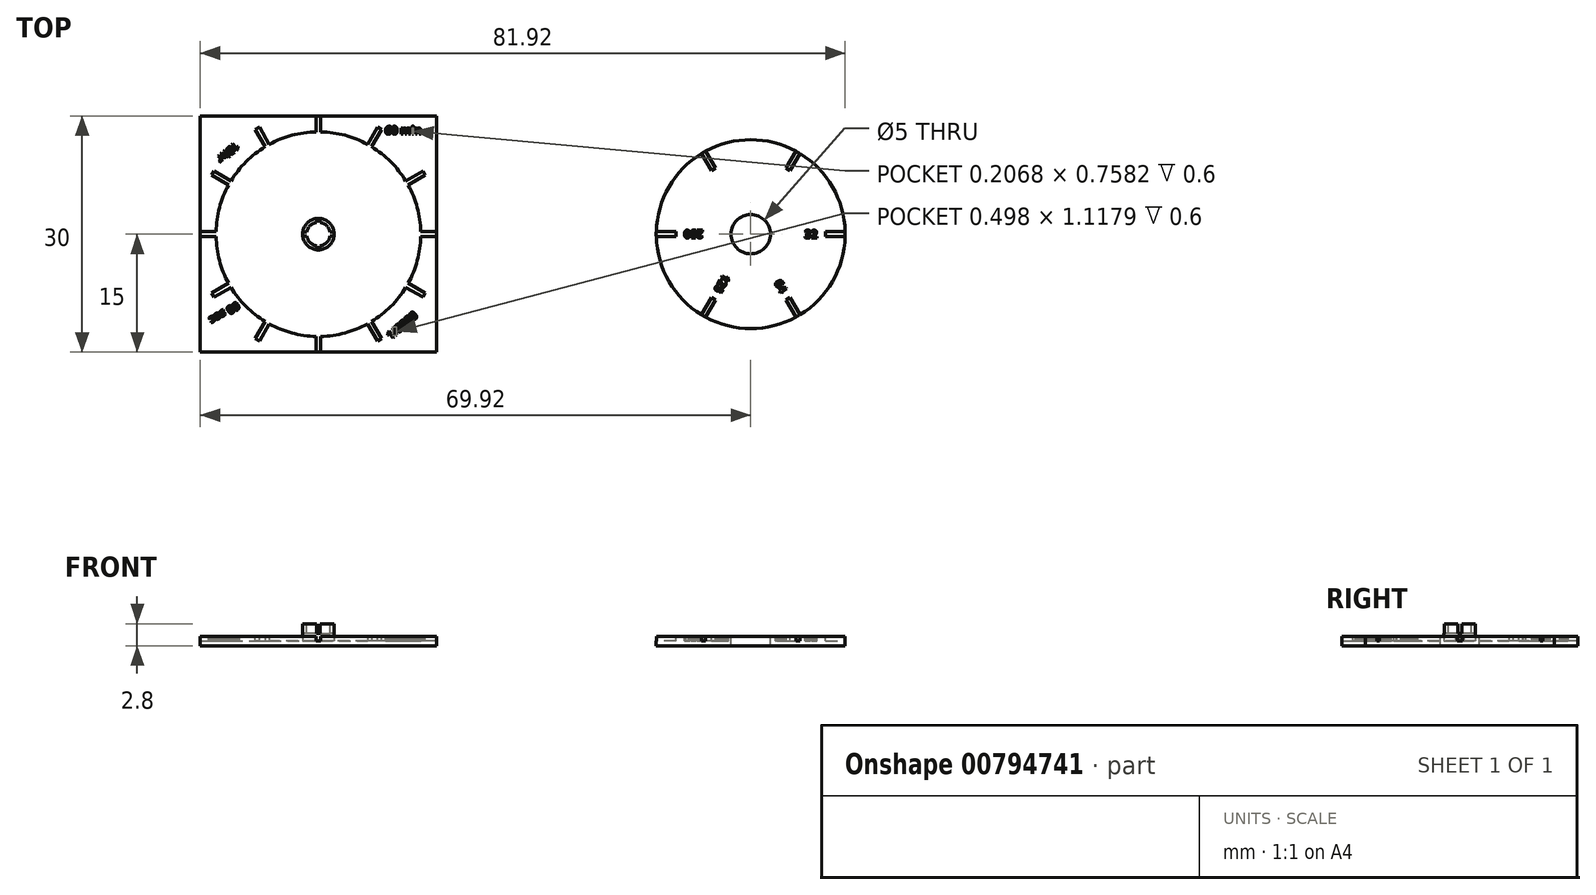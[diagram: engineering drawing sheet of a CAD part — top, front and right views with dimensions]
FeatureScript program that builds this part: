
annotation { "Feature Type Name" : "Feature", "Feature Type Description" : "" }
export const myFeature = defineFeature(function(context is Context, id is Id, definition is map)
    precondition{}
    {
        {
            var Q0;
            Q0=qCreatedBy(makeId("Top.planeOp"),FACE);
            var sketch = newSketch(context, id + "F0", { "sketchPlane" : qUnion([Q0])});
            skLineSegment(sketch, "E0.bottom", {"start": v(-15, 15) * mm, "end": v(15, 15) * mm});
            skLineSegment(sketch, "E0.top", {"start": v(-15, -15) * mm, "end": v(15, -15) * mm});
            skLineSegment(sketch, "E0.left", {"start": v(-15, 15) * mm, "end": v(-15, -15) * mm});
            skLineSegment(sketch, "E0.right", {"start": v(15, 15) * mm, "end": v(15, -15) * mm});
            skPoint(sketch, "E0.middle", {"position": v(0, 0) * mm});
            skCircle(sketch, "E1", {"center": v(0, 0) * mm, "radius": 13 * mm});
            skCircle(sketch, "E2", {"center": v(0, 0) * mm, "radius": 2 * mm});
            skCircle(sketch, "E3", {"center": v(54.92, 0) * mm, "radius": 12 * mm});
            skCircle(sketch, "E4", {"center": v(54.92, 0) * mm, "radius": 2.5 * mm});
            skSolve(sketch);
        }
        {
            var Q0;
            Q0=makeQuery(id+"F0.imprint","IMPRINT",FACE,{"disambiguationData":[TD([[makeQuery(id+"F0.imprint","IMPRINT",EDGE,{"derivedFrom":sQuery(id+"F0.wireOp",EDGE,"E0.bottom")}),-1.0]])]});
            var Q1;
            Q1=makeQuery(id+"F0.imprint","IMPRINT",FACE,{"disambiguationData":[TD([[makeQuery(id+"F0.imprint","IMPRINT",EDGE,{"derivedFrom":sQuery(id+"F0.wireOp",EDGE,"E1")}),1.0]])]});
            var Q2;
            Q2=makeQuery(id+"F0.imprint","IMPRINT",FACE,{"disambiguationData":[TD([[makeQuery(id+"F0.imprint","IMPRINT",EDGE,{"derivedFrom":sQuery(id+"F0.wireOp",EDGE,"E2")}),1.0]])]});
            var Q3;
            Q3=makeQuery(id+"F0.imprint","IMPRINT",FACE,{"disambiguationData":[TD([[makeQuery(id+"F0.imprint","IMPRINT",EDGE,{"derivedFrom":sQuery(id+"F0.wireOp",EDGE,"E3")}),1.0]])]});
            extrude(context, id + "F1", {"entities" : qUnion([Q0, Q1, Q2, Q3]), "oppositeDirection" : true, "depth" : 0.6 * mm, "offsetDistance" : 25 * mm});
        }
        {
            var Q0;
            Q0=makeQuery(id+"F0.imprint","IMPRINT",FACE,{"disambiguationData":[TD([[makeQuery(id+"F0.imprint","IMPRINT",EDGE,{"derivedFrom":sQuery(id+"F0.wireOp",EDGE,"E0.bottom")}),-1.0]])]});
            var Q1;
            Q1=makeQuery(id+"F0.imprint","IMPRINT",FACE,{"disambiguationData":[TD([[makeQuery(id+"F0.imprint","IMPRINT",EDGE,{"derivedFrom":sQuery(id+"F0.wireOp",EDGE,"E3")}),1.0]])]});
            extrude(context, id + "F2", {"entities" : qUnion([Q0, Q1]), "operationType" : NewBodyOperationType.ADD, "depth" : 0.6 * mm, "offsetDistance" : 25 * mm});
        }
        {
            var Q0;
            Q0=makeQuery(id+"F0.imprint","IMPRINT",FACE,{"disambiguationData":[TD([[makeQuery(id+"F0.imprint","IMPRINT",EDGE,{"derivedFrom":sQuery(id+"F0.wireOp",EDGE,"E2")}),1.0]])]});
            var Q1;
            Q1=makeQuery(id+"F1.opExtrude","CAP_FACE",FACE,{"disambiguationData":[OSD([sQuery(id+"F0.wireOp",EDGE,"E0.bottom"),sQuery(id+"F0.wireOp",EDGE,"E0.top"),sQuery(id+"F0.wireOp",EDGE,"E0.left"),sQuery(id+"F0.wireOp",EDGE,"E0.right")])],"isStart":false});
            extrude(context, id + "F3", {"entities" : qUnion([Q0]), "operationType" : NewBodyOperationType.ADD, "depth" : 2.2 * mm, "offsetDistance" : 25 * mm, "hasSecondDirection" : true, "secondDirectionBound" : SecondDirectionBoundingType.UP_TO_SURFACE, "secondDirectionOppositeDirection" : true, "secondDirectionDepth" : 0.29 * mm, "secondDirectionBoundEntityFace" : qUnion([Q1])});
        }
        {
            var Q0;
            Q0=makeQuery(id+"F3.opExtrude","CAP_FACE",FACE,{"disambiguationData":[OSD([sQuery(id+"F0.wireOp",EDGE,"E2")])],"isStart":false});
            var sketch = newSketch(context, id + "F4", { "sketchPlane" : qUnion([Q0])});
            skLineSegment(sketch, "E5.bottom", {"start": v(5, 0.25) * mm, "end": v(-5, 0.25) * mm});
            skLineSegment(sketch, "E5.top", {"start": v(5, -0.25) * mm, "end": v(-5, -0.25) * mm});
            skLineSegment(sketch, "E5.left", {"start": v(5, 0.25) * mm, "end": v(5, -0.25) * mm});
            skLineSegment(sketch, "E5.right", {"start": v(-5, 0.25) * mm, "end": v(-5, -0.25) * mm});
            skPoint(sketch, "E5.middle", {"position": v(0, 0) * mm});
            skLineSegment(sketch, "E6.bottom", {"start": v(0.25, 5) * mm, "end": v(-0.25, 5) * mm});
            skLineSegment(sketch, "E6.top", {"start": v(0.25, -5) * mm, "end": v(-0.25, -5) * mm});
            skLineSegment(sketch, "E6.left", {"start": v(0.25, 5) * mm, "end": v(0.25, -5) * mm});
            skLineSegment(sketch, "E6.right", {"start": v(-0.25, 5) * mm, "end": v(-0.25, -5) * mm});
            skCircle(sketch, "E7", {"center": v(0, 0) * mm, "radius": 1.5 * mm});
            skSolve(sketch);
        }
        {
            var Q0;
            Q0 = qSketchRegion(id + "F4", true);
            var Q1;
            {var subQ0=sQuery(id+"F4.wireOp",EDGE,"E6.left");var subQ1=sQuery(id+"F4.wireOp",EDGE,"E5.bottom");var subQ2=makeQuery(id+"F4.imprint","INTERSECT",VERTEX,{"derivedFrom":[subQ1,subQ0]});Q1=makeQuery(id+"F4.imprint","IMPRINT",FACE,{"disambiguationData":[TD([[makeQuery(id+"F4.imprint","IMPRINT",EDGE,{"disambiguationData":[TD([[subQ2,-1.0]])],"derivedFrom":subQ1}),1.0]])]});}
            extrude(context, id + "F5", {"entities" : qUnion([Q0, Q1]), "operationType" : NewBodyOperationType.REMOVE, "oppositeDirection" : true, "depth" : 1.2 * mm, "offsetDistance" : 25 * mm});
        }
        {
            var Q0;
            Q0=makeQuery(id+"F2.opExtrude","CAP_FACE",FACE,{"disambiguationData":[OSD([sQuery(id+"F0.wireOp",EDGE,"E0.bottom"),sQuery(id+"F0.wireOp",EDGE,"E0.top"),sQuery(id+"F0.wireOp",EDGE,"E0.left"),sQuery(id+"F0.wireOp",EDGE,"E0.right"),sQuery(id+"F0.wireOp",EDGE,"E1")])],"isStart":false});
            var sketch = newSketch(context, id + "F6", { "sketchPlane" : qUnion([Q0])});
            skLineSegment(sketch, "E8.bottom", {"start": v(10.5, 0.3) * mm, "end": v(15.5, 0.3) * mm});
            skLineSegment(sketch, "E8.top", {"start": v(10.5, -0.3) * mm, "end": v(15.5, -0.3) * mm});
            skLineSegment(sketch, "E8.left", {"start": v(10.5, 0.3) * mm, "end": v(10.5, -0.3) * mm});
            skLineSegment(sketch, "E8.right", {"start": v(15.5, 0.3) * mm, "end": v(15.5, -0.3) * mm});
            skPoint(sketch, "E8.middle", {"position": v(13, 0) * mm});
            skLineSegment(sketch, "E9.1.0", {"start": v(9.24, 5) * mm, "end": v(13.57, 7.5) * mm});
            skLineSegment(sketch, "E9.1.1", {"start": v(8.94, 5.5) * mm, "end": v(13.27, 8) * mm});
            skLineSegment(sketch, "E9.1.2", {"start": v(8.94, 5.5) * mm, "end": v(9.24, 5) * mm});
            skLineSegment(sketch, "E9.1.3", {"start": v(13.27, 8) * mm, "end": v(13.57, 7.5) * mm});
            skLineSegment(sketch, "E9.2.0", {"start": v(5.5, 8.94) * mm, "end": v(8, 13.27) * mm});
            skLineSegment(sketch, "E9.2.1", {"start": v(5, 9.24) * mm, "end": v(7.5, 13.57) * mm});
            skLineSegment(sketch, "E9.2.2", {"start": v(5, 9.24) * mm, "end": v(5.5, 8.94) * mm});
            skLineSegment(sketch, "E9.2.3", {"start": v(7.5, 13.57) * mm, "end": v(8, 13.27) * mm});
            skLineSegment(sketch, "E9.3.0", {"start": v(0.3, 10.5) * mm, "end": v(0.3, 15.5) * mm});
            skLineSegment(sketch, "E9.3.1", {"start": v(-0.3, 10.5) * mm, "end": v(-0.3, 15.5) * mm});
            skLineSegment(sketch, "E9.3.2", {"start": v(-0.3, 10.5) * mm, "end": v(0.3, 10.5) * mm});
            skLineSegment(sketch, "E9.3.3", {"start": v(-0.3, 15.5) * mm, "end": v(0.3, 15.5) * mm});
            skLineSegment(sketch, "E9.4.0", {"start": v(-5, 9.24) * mm, "end": v(-7.5, 13.57) * mm});
            skLineSegment(sketch, "E9.4.1", {"start": v(-5.5, 8.94) * mm, "end": v(-8, 13.27) * mm});
            skLineSegment(sketch, "E9.4.2", {"start": v(-5.5, 8.94) * mm, "end": v(-5, 9.24) * mm});
            skLineSegment(sketch, "E9.4.3", {"start": v(-8, 13.27) * mm, "end": v(-7.5, 13.57) * mm});
            skLineSegment(sketch, "E9.5.0", {"start": v(-8.94, 5.5) * mm, "end": v(-13.27, 8) * mm});
            skLineSegment(sketch, "E9.5.1", {"start": v(-9.24, 5) * mm, "end": v(-13.57, 7.5) * mm});
            skLineSegment(sketch, "E9.5.2", {"start": v(-9.24, 5) * mm, "end": v(-8.94, 5.5) * mm});
            skLineSegment(sketch, "E9.5.3", {"start": v(-13.57, 7.5) * mm, "end": v(-13.27, 8) * mm});
            skLineSegment(sketch, "E9.6.0", {"start": v(-10.5, 0.3) * mm, "end": v(-15.5, 0.3) * mm});
            skLineSegment(sketch, "E9.6.1", {"start": v(-10.5, -0.3) * mm, "end": v(-15.5, -0.3) * mm});
            skLineSegment(sketch, "E9.6.2", {"start": v(-10.5, -0.3) * mm, "end": v(-10.5, 0.3) * mm});
            skLineSegment(sketch, "E9.6.3", {"start": v(-15.5, -0.3) * mm, "end": v(-15.5, 0.3) * mm});
            skLineSegment(sketch, "E9.7.0", {"start": v(-9.24, -5) * mm, "end": v(-13.57, -7.5) * mm});
            skLineSegment(sketch, "E9.7.1", {"start": v(-8.94, -5.5) * mm, "end": v(-13.27, -8) * mm});
            skLineSegment(sketch, "E9.7.2", {"start": v(-8.94, -5.5) * mm, "end": v(-9.24, -5) * mm});
            skLineSegment(sketch, "E9.7.3", {"start": v(-13.27, -8) * mm, "end": v(-13.57, -7.5) * mm});
            skLineSegment(sketch, "E9.8.0", {"start": v(-5.5, -8.94) * mm, "end": v(-8, -13.27) * mm});
            skLineSegment(sketch, "E9.8.1", {"start": v(-5, -9.24) * mm, "end": v(-7.5, -13.57) * mm});
            skLineSegment(sketch, "E9.8.2", {"start": v(-5, -9.24) * mm, "end": v(-5.5, -8.94) * mm});
            skLineSegment(sketch, "E9.8.3", {"start": v(-7.5, -13.57) * mm, "end": v(-8, -13.27) * mm});
            skLineSegment(sketch, "E9.9.0", {"start": v(-0.3, -10.5) * mm, "end": v(-0.3, -15.5) * mm});
            skLineSegment(sketch, "E9.9.1", {"start": v(0.3, -10.5) * mm, "end": v(0.3, -15.5) * mm});
            skLineSegment(sketch, "E9.9.2", {"start": v(0.3, -10.5) * mm, "end": v(-0.3, -10.5) * mm});
            skLineSegment(sketch, "E9.9.3", {"start": v(0.3, -15.5) * mm, "end": v(-0.3, -15.5) * mm});
            skLineSegment(sketch, "E9.10.0", {"start": v(5, -9.24) * mm, "end": v(7.5, -13.57) * mm});
            skLineSegment(sketch, "E9.10.1", {"start": v(5.5, -8.94) * mm, "end": v(8, -13.27) * mm});
            skLineSegment(sketch, "E9.10.2", {"start": v(5.5, -8.94) * mm, "end": v(5, -9.24) * mm});
            skLineSegment(sketch, "E9.10.3", {"start": v(8, -13.27) * mm, "end": v(7.5, -13.57) * mm});
            skLineSegment(sketch, "E9.11.0", {"start": v(8.94, -5.5) * mm, "end": v(13.27, -8) * mm});
            skLineSegment(sketch, "E9.11.1", {"start": v(9.24, -5) * mm, "end": v(13.57, -7.5) * mm});
            skLineSegment(sketch, "E9.11.2", {"start": v(9.24, -5) * mm, "end": v(8.94, -5.5) * mm});
            skLineSegment(sketch, "E9.11.3", {"start": v(13.57, -7.5) * mm, "end": v(13.27, -8) * mm});
            skPoint(sketch, "E9.center", {"position": v(0, 0) * mm});
            skSolve(sketch);
        }
        {
            var Q0;
            Q0 = qSketchRegion(id + "F6", true);
            var Q1;
            Q1=makeQuery(id+"F1.opExtrude","CAP_FACE",FACE,{"disambiguationData":[OSD([sQuery(id+"F0.wireOp",EDGE,"E0.bottom"),sQuery(id+"F0.wireOp",EDGE,"E0.top"),sQuery(id+"F0.wireOp",EDGE,"E0.left"),sQuery(id+"F0.wireOp",EDGE,"E0.right")])],"isStart":true});
            extrude(context, id + "F7", {"entities" : qUnion([Q0]), "operationType" : NewBodyOperationType.REMOVE, "endBound" : BoundingType.UP_TO_SURFACE, "oppositeDirection" : true, "depth" : 25 * mm, "endBoundEntityFace" : qUnion([Q1]), "offsetDistance" : 25 * mm});
        }
        {
            var Q0;
            Q0=makeQuery(id+"F2.opExtrude","CAP_FACE",FACE,{"disambiguationData":[OSD([sQuery(id+"F0.wireOp",EDGE,"E3"),sQuery(id+"F0.wireOp",EDGE,"E4")])],"isStart":false});
            var sketch = newSketch(context, id + "F8", { "sketchPlane" : qUnion([Q0])});
            skLineSegment(sketch, "E10.bottom", {"start": v(64.42, 0.3) * mm, "end": v(69.42, 0.3) * mm});
            skLineSegment(sketch, "E10.top", {"start": v(64.42, -0.3) * mm, "end": v(69.42, -0.3) * mm});
            skLineSegment(sketch, "E10.left", {"start": v(64.42, 0.3) * mm, "end": v(64.42, -0.3) * mm});
            skLineSegment(sketch, "E10.right", {"start": v(69.42, 0.3) * mm, "end": v(69.42, -0.3) * mm});
            skPoint(sketch, "E10.middle", {"position": v(66.92, 0) * mm});
            skLineSegment(sketch, "E11.1.0", {"start": v(59.93, 8.08) * mm, "end": v(62.43, 12.4) * mm});
            skLineSegment(sketch, "E11.1.1", {"start": v(59.41, 8.38) * mm, "end": v(61.91, 12.7) * mm});
            skPoint(sketch, "E11.1.2", {"position": v(60.92, 10.4) * mm});
            skLineSegment(sketch, "E11.1.3", {"start": v(61.91, 12.7) * mm, "end": v(62.43, 12.4) * mm});
            skLineSegment(sketch, "E11.1.4", {"start": v(59.41, 8.38) * mm, "end": v(59.93, 8.08) * mm});
            skLineSegment(sketch, "E11.2.0", {"start": v(50.43, 8.38) * mm, "end": v(47.93, 12.7) * mm});
            skLineSegment(sketch, "E11.2.1", {"start": v(49.91, 8.08) * mm, "end": v(47.41, 12.4) * mm});
            skPoint(sketch, "E11.2.2", {"position": v(48.92, 10.4) * mm});
            skLineSegment(sketch, "E11.2.3", {"start": v(47.41, 12.4) * mm, "end": v(47.93, 12.7) * mm});
            skLineSegment(sketch, "E11.2.4", {"start": v(49.91, 8.08) * mm, "end": v(50.43, 8.38) * mm});
            skLineSegment(sketch, "E11.3.0", {"start": v(45.42, 0.3) * mm, "end": v(40.42, 0.3) * mm});
            skLineSegment(sketch, "E11.3.1", {"start": v(45.42, -0.3) * mm, "end": v(40.42, -0.3) * mm});
            skPoint(sketch, "E11.3.2", {"position": v(42.92, 0) * mm});
            skLineSegment(sketch, "E11.3.3", {"start": v(40.42, -0.3) * mm, "end": v(40.42, 0.3) * mm});
            skLineSegment(sketch, "E11.3.4", {"start": v(45.42, -0.3) * mm, "end": v(45.42, 0.3) * mm});
            skLineSegment(sketch, "E11.4.0", {"start": v(49.91, -8.08) * mm, "end": v(47.41, -12.4) * mm});
            skLineSegment(sketch, "E11.4.1", {"start": v(50.43, -8.38) * mm, "end": v(47.93, -12.7) * mm});
            skPoint(sketch, "E11.4.2", {"position": v(48.92, -10.4) * mm});
            skLineSegment(sketch, "E11.4.3", {"start": v(47.93, -12.7) * mm, "end": v(47.41, -12.4) * mm});
            skLineSegment(sketch, "E11.4.4", {"start": v(50.43, -8.38) * mm, "end": v(49.91, -8.08) * mm});
            skLineSegment(sketch, "E11.5.0", {"start": v(59.41, -8.38) * mm, "end": v(61.91, -12.7) * mm});
            skLineSegment(sketch, "E11.5.1", {"start": v(59.93, -8.08) * mm, "end": v(62.43, -12.4) * mm});
            skPoint(sketch, "E11.5.2", {"position": v(60.92, -10.4) * mm});
            skLineSegment(sketch, "E11.5.3", {"start": v(62.43, -12.4) * mm, "end": v(61.91, -12.7) * mm});
            skLineSegment(sketch, "E11.5.4", {"start": v(59.93, -8.08) * mm, "end": v(59.41, -8.38) * mm});
            skPoint(sketch, "E11.center", {"position": v(54.92, 0) * mm});
            skSolve(sketch);
        }
        {
            var Q0;
            Q0 = qSketchRegion(id + "F8", true);
            extrude(context, id + "F9", {"entities" : qUnion([Q0]), "operationType" : NewBodyOperationType.REMOVE, "oppositeDirection" : true, "depth" : 0.6 * mm, "offsetDistance" : 25 * mm});
        }
        {
            var Q0;
            Q0=makeQuery(id+"F2.opExtrude","CAP_FACE",FACE,{"disambiguationData":[OSD([sQuery(id+"F0.wireOp",EDGE,"E3"),sQuery(id+"F0.wireOp",EDGE,"E4")])],"isStart":false});
            var sketch = newSketch(context, id + "F10", { "sketchPlane" : qUnion([Q0])});
            skText(sketch, "E12", { "text": "32", "fontName": "OpenSans-Bold.ttf"});
            skText(sketch, "E13", { "text": "64", "fontName": "OpenSans-Bold.ttf"});
            skPoint(sketch, "E14", {"position": v(59.17, -7.36) * mm});
            skLineSegment(sketch, "E15", {"start": v(59.17, -7.36) * mm, "end": v(59.67, -8.23) * mm, "construction": true});
            skText(sketch, "E16", { "text": "125", "fontName": "OpenSans-Bold.ttf"});
            skLineSegment(sketch, "E17", {"start": v(50.67, -7.36) * mm, "end": v(50.17, -8.23) * mm, "construction": true});
            skText(sketch, "E18", { "text": "250", "fontName": "OpenSans-Bold.ttf"});
            skLineSegment(sketch, "E19", {"start": v(46.42, 0) * mm, "end": v(45.42, 0) * mm, "construction": true});
            const initialGuessF10  = {"E12": [0.06179, -0.0005, 1, 0, 0.001], "E13": [0.05791, -0.00618, 0.5, -0.86603, 0.001], "E16": [0.05144, -0.00503, -0.5, -0.86603, 0.001], "E18": [0.04884, 0.0005, -1, 0, 0.001]};
            skSetInitialGuess(sketch, initialGuessF10);
            skSolve(sketch);
        }
        {
            var Q0;
            Q0 = qSketchRegion(id + "F10", true);
            var Q1;
            Q1=makeQuery(id+"F9.boolean.opBoolean","COPY",FACE,{"derivedFrom":makeQuery(id+"F9.opExtrude","CAP_FACE",FACE,{"disambiguationData":[OSD([sQuery(id+"F8.wireOp",EDGE,"E11.3.0"),sQuery(id+"F8.wireOp",EDGE,"E11.3.1"),sQuery(id+"F8.wireOp",EDGE,"E11.3.3"),sQuery(id+"F8.wireOp",EDGE,"E11.3.4")])],"isStart":false})});
            extrude(context, id + "F11", {"entities" : qUnion([Q0]), "operationType" : NewBodyOperationType.REMOVE, "endBound" : BoundingType.UP_TO_SURFACE, "oppositeDirection" : true, "depth" : 25 * mm, "endBoundEntityFace" : qUnion([Q1]), "offsetDistance" : 25 * mm});
        }
        {
            var Q0;
            {var subQ0=sQuery(id+"F0.wireOp",EDGE,"E1");var subQ1=sQuery(id+"F0.wireOp",EDGE,"E0.right");var subQ2=sQuery(id+"F0.wireOp",EDGE,"E0.bottom");Q0=makeQuery(id+"F7.boolean.opBoolean","SPLIT",FACE,{"disambiguationData":[TD([makeQuery(id+"F7.opExtrude","SWEPT_FACE",FACE,{"disambiguationData":[OSD([sQuery(id+"F6.wireOp",EDGE,"E8.bottom")])]})])],"derivedFrom":makeQuery(id+"F2.opExtrude","CAP_FACE",FACE,{"disambiguationData":[OSD([subQ2,sQuery(id+"F0.wireOp",EDGE,"E0.top"),sQuery(id+"F0.wireOp",EDGE,"E0.left"),subQ1,subQ0])],"isStart":false})});}
            var sketch = newSketch(context, id + "F12", { "sketchPlane" : qUnion([Q0])});
            skText(sketch, "E20", { "text": "60 min", "fontName": "OpenSans-Bold.ttf"});
            skText(sketch, "E21", { "text": "1/8000", "fontName": "OpenSans-Bold.ttf"});
            skText(sketch, "E22", { "text": "60 sec", "fontName": "OpenSans-Bold.ttf"});
            skText(sketch, "E23", { "text": "15hr", "fontName": "OpenSans-Bold.ttf"});
            const initialGuessF12  = {"E20": [0.00848, 0.0127, 1, 0, 0.001], "E21": [0.00919, -0.01342, 0.76604, 0.64279, 0.001], "E22": [-0.01038, -0.00856, -0.86603, -0.5, 0.001], "E23": [-0.0106, 0.01174, -0.76604, -0.64279, 0.001]};
            skSetInitialGuess(sketch, initialGuessF12);
            skSolve(sketch);
        }
        {
            var Q0;
            Q0 = qSketchRegion(id + "F12", true);
            var Q1;
            {var subQ0=sQuery(id+"F0.wireOp",EDGE,"E0.right");var subQ1=sQuery(id+"F0.wireOp",EDGE,"E0.left");var subQ2=sQuery(id+"F0.wireOp",EDGE,"E0.top");var subQ3=sQuery(id+"F0.wireOp",EDGE,"E0.bottom");Q1=makeQuery(id+"F7.boolean.opBoolean","MERGE",FACE,{"derivedFrom":[makeQuery(id+"F1.opExtrude","CAP_FACE",FACE,{"disambiguationData":[OSD([subQ3,subQ2,subQ1,subQ0])],"isStart":true}),makeQuery(id+"F7.opExtrude","CAP_FACE",FACE,{"disambiguationData":[OSD([subQ3,subQ2,subQ1,subQ0])],"isStart":false})]});}
            extrude(context, id + "F13", {"entities" : qUnion([Q0]), "operationType" : NewBodyOperationType.REMOVE, "endBound" : BoundingType.UP_TO_SURFACE, "oppositeDirection" : true, "depth" : 25 * mm, "endBoundEntityFace" : qUnion([Q1]), "offsetDistance" : 25 * mm});
        }
    });
